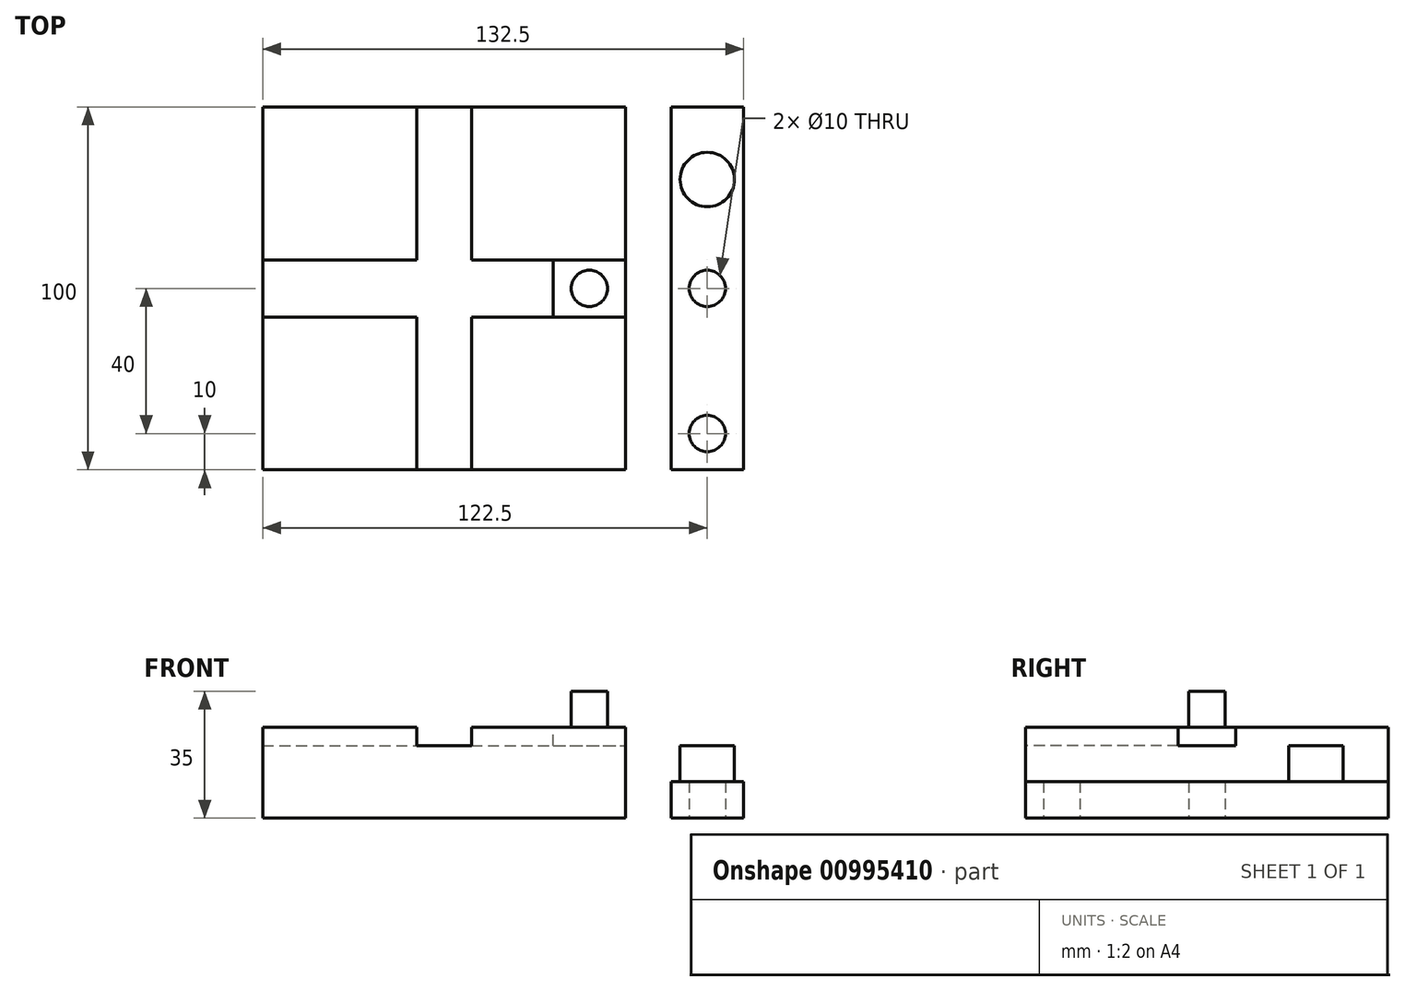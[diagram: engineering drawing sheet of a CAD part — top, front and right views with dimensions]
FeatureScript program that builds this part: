
annotation { "Feature Type Name" : "Feature", "Feature Type Description" : "" }
export const myFeature = defineFeature(function(context is Context, id is Id, definition is map)
    precondition{}
    {
        {
            var Q0;
            Q0=qCreatedBy(makeId("Top.planeOp"),FACE);
            var sketch = newSketch(context, id + "F0", { "sketchPlane" : qUnion([Q0])});
            skLineSegment(sketch, "E0.bottom", {"start": v(50, -50) * mm, "end": v(-50, -50) * mm});
            skLineSegment(sketch, "E0.top", {"start": v(50, 50) * mm, "end": v(-50, 50) * mm});
            skLineSegment(sketch, "E0.left", {"start": v(50, -50) * mm, "end": v(50, 50) * mm});
            skLineSegment(sketch, "E0.right", {"start": v(-50, -50) * mm, "end": v(-50, 50) * mm});
            skPoint(sketch, "E0.middle", {"position": v(0, 0) * mm});
            skSolve(sketch);
        }
        {
            var Q0;
            Q0=makeQuery(id+"F0.imprint","IMPRINT",FACE,{"disambiguationData":[TD([[makeQuery(id+"F0.imprint","IMPRINT",EDGE,{"derivedFrom":sQuery(id+"F0.wireOp",EDGE,"E0.bottom")}),-1.0]])]});
            extrude(context, id + "F1", {"entities" : qUnion([Q0]), "depth" : 25 * mm, "offsetDistance" : 25 * mm});
        }
        {
            var Q0;
            Q0=makeQuery(id+"F1.opExtrude","SWEPT_FACE",FACE,{"disambiguationData":[OSD([sQuery(id+"F0.wireOp",EDGE,"E0.left")])]});
            var sketch = newSketch(context, id + "F2", { "sketchPlane" : qUnion([Q0])});
            skLineSegment(sketch, "E1.bottom", {"start": v(-7.88, 20) * mm, "end": v(7.88, 20) * mm});
            skLineSegment(sketch, "E1.top", {"start": v(-7.88, 30) * mm, "end": v(7.88, 30) * mm});
            skLineSegment(sketch, "E1.left", {"start": v(-7.88, 20) * mm, "end": v(-7.88, 30) * mm});
            skLineSegment(sketch, "E1.right", {"start": v(7.88, 20) * mm, "end": v(7.88, 30) * mm});
            skPoint(sketch, "E1.middle", {"position": v(0, 25) * mm});
            skSolve(sketch);
        }
        {
            var Q0;
            {var subQ0=sQuery(id+"F2.wireOp",EDGE,"E1.bottom");Q0=makeQuery(id+"F2.imprint","IMPRINT",FACE,{"disambiguationData":[TD([[makeQuery(id+"F2.imprint","IMPRINT",EDGE,{"derivedFrom":subQ0}),1.0]])]});}
            var Q1;
            Q1=makeQuery(id+"F1.opExtrude","SWEPT_FACE",FACE,{"disambiguationData":[OSD([sQuery(id+"F0.wireOp",EDGE,"E0.right")])]});
            extrude(context, id + "F3", {"entities" : qUnion([Q0]), "operationType" : NewBodyOperationType.REMOVE, "endBound" : BoundingType.UP_TO_SURFACE, "oppositeDirection" : true, "depth" : 25 * mm, "endBoundEntityFace" : qUnion([Q1]), "offsetDistance" : 25 * mm});
        }
        {
            var Q0;
            Q0=makeQuery(id+"F1.opExtrude","SWEPT_FACE",FACE,{"disambiguationData":[OSD([sQuery(id+"F0.wireOp",EDGE,"E0.bottom")])]});
            var sketch = newSketch(context, id + "F4", { "sketchPlane" : qUnion([Q0])});
            skLineSegment(sketch, "E2.bottom", {"start": v(-7.5, 20) * mm, "end": v(7.5, 20) * mm});
            skLineSegment(sketch, "E2.top", {"start": v(-7.5, 30) * mm, "end": v(7.5, 30) * mm});
            skLineSegment(sketch, "E2.left", {"start": v(-7.5, 20) * mm, "end": v(-7.5, 30) * mm});
            skLineSegment(sketch, "E2.right", {"start": v(7.5, 20) * mm, "end": v(7.5, 30) * mm});
            skPoint(sketch, "E2.middle", {"position": v(0, 25) * mm});
            skSolve(sketch);
        }
        {
            var Q0;
            {var subQ0=sQuery(id+"F4.wireOp",EDGE,"E2.bottom");Q0=makeQuery(id+"F4.imprint","IMPRINT",FACE,{"disambiguationData":[TD([[makeQuery(id+"F4.imprint","IMPRINT",EDGE,{"derivedFrom":subQ0}),1.0]])]});}
            var Q1;
            Q1=makeQuery(id+"F1.opExtrude","SWEPT_FACE",FACE,{"disambiguationData":[OSD([sQuery(id+"F0.wireOp",EDGE,"E0.top")])]});
            extrude(context, id + "F5", {"entities" : qUnion([Q0]), "operationType" : NewBodyOperationType.REMOVE, "endBound" : BoundingType.UP_TO_SURFACE, "oppositeDirection" : true, "depth" : 25 * mm, "endBoundEntityFace" : qUnion([Q1]), "offsetDistance" : 25 * mm});
        }
        {
            var Q0;
            {var subQ0=sQuery(id+"F2.wireOp",EDGE,"E1.bottom");Q0=makeQuery(id+"F2.imprint","IMPRINT",FACE,{"disambiguationData":[TD([[makeQuery(id+"F2.imprint","IMPRINT",EDGE,{"derivedFrom":subQ0}),1.0]])]});}
            extrude(context, id + "F6", {"entities" : qUnion([Q0]), "oppositeDirection" : true, "depth" : 20 * mm, "offsetDistance" : 25 * mm});
        }
        {
            var Q0;
            Q0=makeQuery(id+"F6.opExtrude","SWEPT_FACE",FACE,{"disambiguationData":[OSD([sQuery(id+"F0.wireOp",EDGE,"E0.left")])]});
            var sketch = newSketch(context, id + "F7", { "sketchPlane" : qUnion([Q0])});
            skCircle(sketch, "E3", {"center": v(40, 0) * mm, "radius": 5 * mm});
            skPoint(sketch, "E3.centerSnap0", {"position": v(30, 0) * mm});
            skPoint(sketch, "E3.centerSnap1", {"position": v(40, -7.88) * mm});
            skSolve(sketch);
        }
        {
            var Q0;
            Q0=makeQuery(id+"F7.imprint","IMPRINT",FACE,{"disambiguationData":[TD([[makeQuery(id+"F7.imprint","IMPRINT",EDGE,{"derivedFrom":sQuery(id+"F7.wireOp",EDGE,"E3")}),1.0]])]});
            extrude(context, id + "F8", {"entities" : qUnion([Q0]), "operationType" : NewBodyOperationType.ADD, "depth" : 10 * mm, "offsetDistance" : 25 * mm});
        }
        {
            var Q0;
            Q0=qCreatedBy(makeId("Top.planeOp"),FACE);
            var sketch = newSketch(context, id + "F9", { "sketchPlane" : qUnion([Q0])});
            skLineSegment(sketch, "E4.bottom", {"start": v(82.5, -50) * mm, "end": v(62.5, -50) * mm});
            skLineSegment(sketch, "E4.top", {"start": v(82.5, 50) * mm, "end": v(62.5, 50) * mm});
            skLineSegment(sketch, "E4.left", {"start": v(82.5, -50) * mm, "end": v(82.5, 50) * mm});
            skLineSegment(sketch, "E4.right", {"start": v(62.5, -50) * mm, "end": v(62.5, 50) * mm});
            skPoint(sketch, "E4.middle", {"position": v(72.5, 0) * mm});
            skCircle(sketch, "E5", {"center": v(72.5, -40) * mm, "radius": 5 * mm});
            skCircle(sketch, "E6", {"center": v(72.5, 0) * mm, "radius": 5 * mm});
            skSolve(sketch);
        }
        {
            var Q0;
            Q0=makeQuery(id+"F9.imprint","IMPRINT",FACE,{"disambiguationData":[TD([[makeQuery(id+"F9.imprint","IMPRINT",EDGE,{"derivedFrom":sQuery(id+"F9.wireOp",EDGE,"E4.bottom")}),-1.0]])]});
            extrude(context, id + "F10", {"entities" : qUnion([Q0]), "depth" : 10 * mm, "offsetDistance" : 25 * mm});
        }
        {
            var Q0;
            Q0=makeQuery(id+"F10.opExtrude","CAP_FACE",FACE,{"disambiguationData":[OSD([sQuery(id+"F9.wireOp",EDGE,"E4.bottom"),sQuery(id+"F9.wireOp",EDGE,"E4.top"),sQuery(id+"F9.wireOp",EDGE,"E4.left"),sQuery(id+"F9.wireOp",EDGE,"E4.right"),sQuery(id+"F9.wireOp",EDGE,"E5"),sQuery(id+"F9.wireOp",EDGE,"E6")])],"isStart":false});
            var sketch = newSketch(context, id + "F11", { "sketchPlane" : qUnion([Q0])});
            skCircle(sketch, "E7", {"center": v(72.5, 30) * mm, "radius": 7.5 * mm});
            skPoint(sketch, "E7.centerSnap0", {"position": v(72.5, 50) * mm});
            skSolve(sketch);
        }
        {
            var Q0;
            Q0=makeQuery(id+"F11.imprint","IMPRINT",FACE,{"disambiguationData":[TD([[makeQuery(id+"F11.imprint","IMPRINT",EDGE,{"derivedFrom":sQuery(id+"F11.wireOp",EDGE,"E7")}),1.0]])]});
            extrude(context, id + "F12", {"entities" : qUnion([Q0]), "operationType" : NewBodyOperationType.ADD, "depth" : 10 * mm, "offsetDistance" : 25 * mm});
        }
    });
